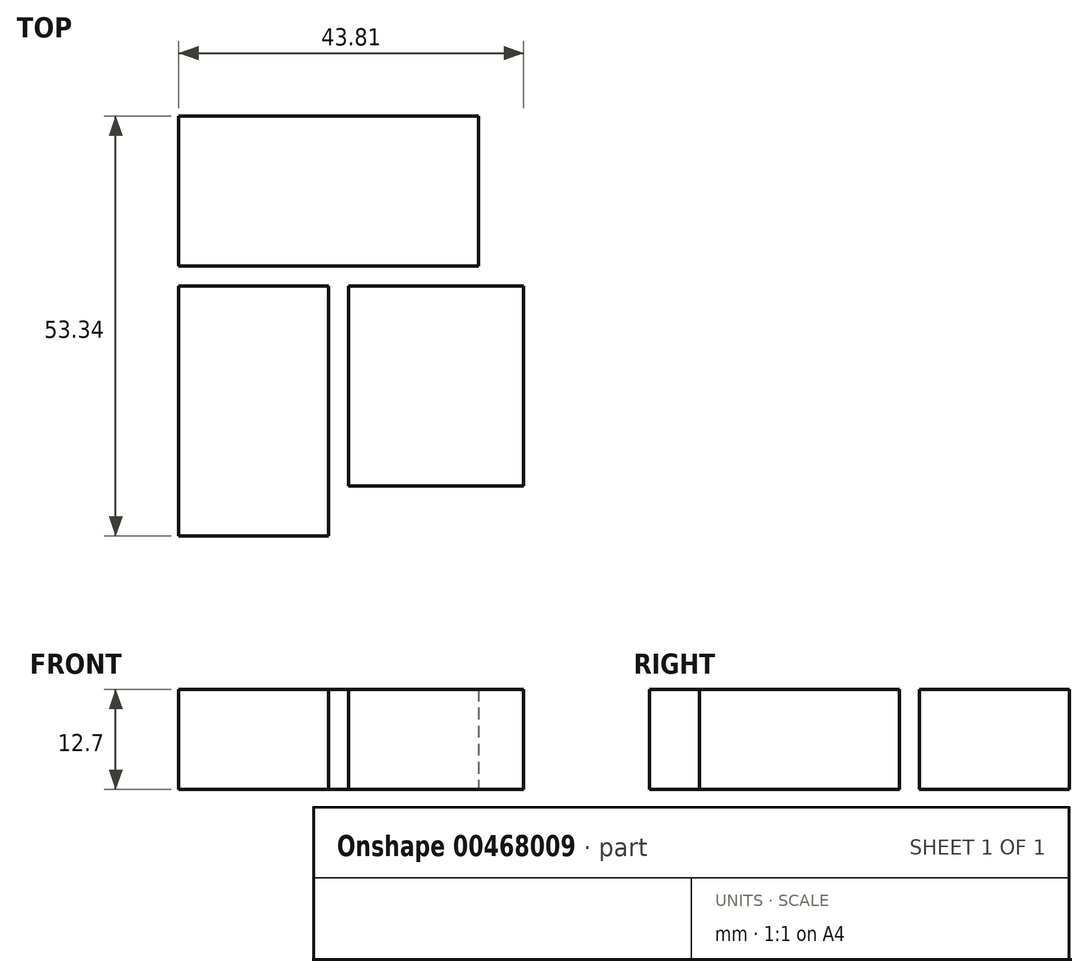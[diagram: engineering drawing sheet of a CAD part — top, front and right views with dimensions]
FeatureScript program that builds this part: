
annotation { "Feature Type Name" : "Feature", "Feature Type Description" : "" }
export const myFeature = defineFeature(function(context is Context, id is Id, definition is map)
    precondition{}
    {
        {
            var Q0;
            Q0=qCreatedBy(makeId("Top.planeOp"),FACE);
            var sketch = newSketch(context, id + "F0", { "sketchPlane" : qUnion([Q0])});
            skLineSegment(sketch, "E0.bottom", {"start": v(0, 0) * mm, "end": v(38.1, 0) * mm});
            skLineSegment(sketch, "E0.top", {"start": v(0, 19.05) * mm, "end": v(38.1, 19.05) * mm});
            skLineSegment(sketch, "E0.left", {"start": v(0, 0) * mm, "end": v(0, 19.05) * mm});
            skLineSegment(sketch, "E0.right", {"start": v(38.1, 0) * mm, "end": v(38.1, 19.05) * mm});
            skLineSegment(sketch, "E1.bottom", {"start": v(43.82, -27.94) * mm, "end": v(21.6, -27.94) * mm});
            skLineSegment(sketch, "E1.top", {"start": v(43.82, -2.54) * mm, "end": v(21.59, -2.54) * mm});
            skLineSegment(sketch, "E1.left", {"start": v(43.82, -27.94) * mm, "end": v(43.81, -2.54) * mm});
            skLineSegment(sketch, "E1.right", {"start": v(21.59, -27.94) * mm, "end": v(21.59, -2.54) * mm});
            skLineSegment(sketch, "E2.bottom", {"start": v(0, -34.3) * mm, "end": v(19.05, -34.3) * mm});
            skLineSegment(sketch, "E2.top", {"start": v(0, -2.54) * mm, "end": v(19.05, -2.54) * mm});
            skLineSegment(sketch, "E2.left", {"start": v(0, -34.3) * mm, "end": v(0, -2.54) * mm});
            skLineSegment(sketch, "E2.right", {"start": v(19.05, -34.3) * mm, "end": v(19.05, -2.54) * mm});
            skSolve(sketch);
        }
        {
            var Q0;
            Q0 = qSketchRegion(id + "F0", true);
            extrude(context, id + "F1", {"entities" : qUnion([Q0]), "depth" : 12.7 * mm});
        }
    });
